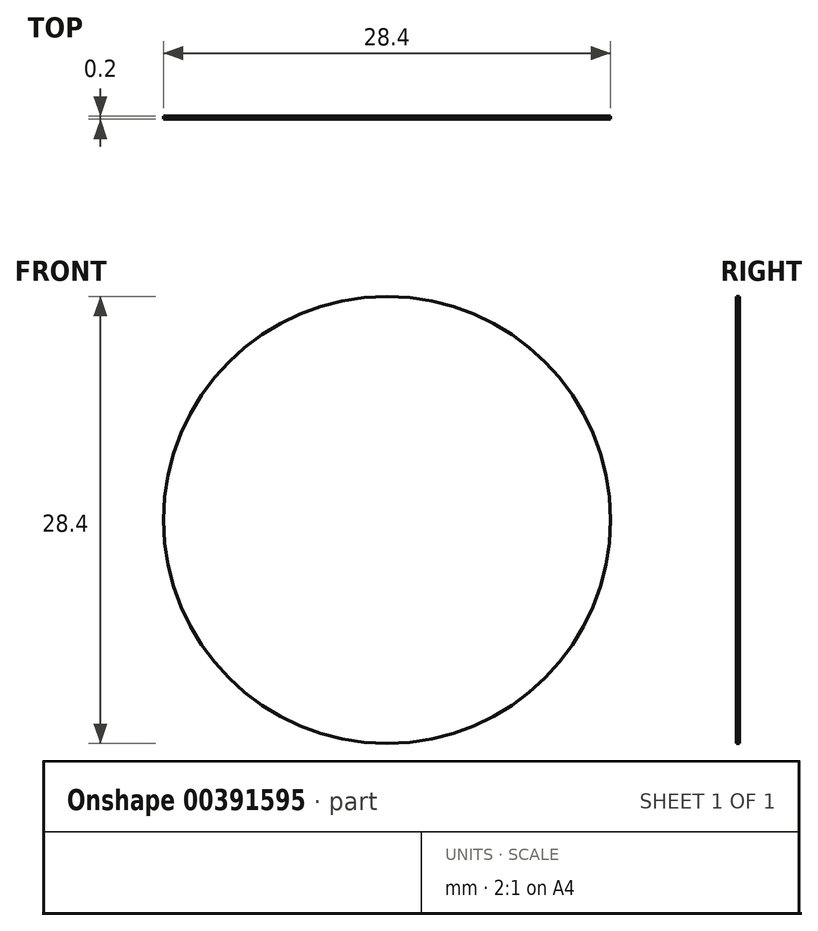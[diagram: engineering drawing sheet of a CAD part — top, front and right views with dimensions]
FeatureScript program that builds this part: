
annotation { "Feature Type Name" : "Feature", "Feature Type Description" : "" }
export const myFeature = defineFeature(function(context is Context, id is Id, definition is map)
    precondition{}
    {
        {
            var Q0;
            Q0=qCreatedBy(makeId("Front.planeOp"),FACE);
            var sketch = newSketch(context, id + "F0", { "sketchPlane" : qUnion([Q0])});
            skCircle(sketch, "E0", {"center": v(0, 0) * mm, "radius": 8 * mm, "construction": true});
            skCircle(sketch, "E1", {"center": v(0, 0) * mm, "radius": 10.5 * mm, "construction": true});
            skLineSegment(sketch, "E2", {"start": v(0, 8) * mm, "end": v(0.75, 8) * mm, "construction": true});
            skLineSegment(sketch, "E3", {"start": v(0.75, 8) * mm, "end": v(0.75, 13.5) * mm, "construction": true});
            skLineSegment(sketch, "E4", {"start": v(0.75, 13.5) * mm, "end": v(0, 13.5) * mm, "construction": true});
            skLineSegment(sketch, "E5", {"start": v(0, 13.5) * mm, "end": v(-0.75, 13.5) * mm, "construction": true});
            skLineSegment(sketch, "E6", {"start": v(-0.75, 13.5) * mm, "end": v(-0.75, 8) * mm, "construction": true});
            skLineSegment(sketch, "E7", {"start": v(-0.75, 8) * mm, "end": v(0, 8) * mm, "construction": true});
            skLineSegment(sketch, "E8.1.0", {"start": v(-3.35, 7.3) * mm, "end": v(-6.1, 12.07) * mm});
            skLineSegment(sketch, "E8.1.1", {"start": v(-7.4, 11.32) * mm, "end": v(-4.65, 6.55) * mm});
            skLineSegment(sketch, "E8.1.2", {"start": v(-4.65, 6.55) * mm, "end": v(-4, 6.93) * mm});
            skLineSegment(sketch, "E8.1.3", {"start": v(-4, 6.93) * mm, "end": v(-3.35, 7.3) * mm});
            skLineSegment(sketch, "E8.1.4", {"start": v(-6.1, 12.07) * mm, "end": v(-6.75, 11.7) * mm});
            skLineSegment(sketch, "E8.1.5", {"start": v(-6.75, 11.7) * mm, "end": v(-7.4, 11.32) * mm});
            skLineSegment(sketch, "E8.2.0", {"start": v(-6.55, 4.65) * mm, "end": v(-11.32, 7.4) * mm});
            skLineSegment(sketch, "E8.2.1", {"start": v(-12.07, 6.1) * mm, "end": v(-7.3, 3.35) * mm});
            skLineSegment(sketch, "E8.2.2", {"start": v(-7.3, 3.35) * mm, "end": v(-6.93, 4) * mm});
            skLineSegment(sketch, "E8.2.3", {"start": v(-6.93, 4) * mm, "end": v(-6.55, 4.65) * mm});
            skLineSegment(sketch, "E8.2.4", {"start": v(-11.32, 7.4) * mm, "end": v(-11.7, 6.75) * mm});
            skLineSegment(sketch, "E8.2.5", {"start": v(-11.7, 6.75) * mm, "end": v(-12.07, 6.1) * mm});
            skLineSegment(sketch, "E8.3.0", {"start": v(-8, 0.75) * mm, "end": v(-13.5, 0.75) * mm, "construction": true});
            skLineSegment(sketch, "E8.3.1", {"start": v(-13.5, -0.75) * mm, "end": v(-8, -0.75) * mm, "construction": true});
            skLineSegment(sketch, "E8.3.2", {"start": v(-8, -0.75) * mm, "end": v(-8, 0) * mm, "construction": true});
            skLineSegment(sketch, "E8.3.3", {"start": v(-8, 0) * mm, "end": v(-8, 0.75) * mm, "construction": true});
            skLineSegment(sketch, "E8.3.4", {"start": v(-13.5, 0.75) * mm, "end": v(-13.5, 0) * mm, "construction": true});
            skLineSegment(sketch, "E8.3.5", {"start": v(-13.5, 0) * mm, "end": v(-13.5, -0.75) * mm, "construction": true});
            skLineSegment(sketch, "E8.4.0", {"start": v(-7.3, -3.35) * mm, "end": v(-12.07, -6.1) * mm});
            skLineSegment(sketch, "E8.4.1", {"start": v(-11.32, -7.4) * mm, "end": v(-6.55, -4.65) * mm});
            skLineSegment(sketch, "E8.4.2", {"start": v(-6.55, -4.65) * mm, "end": v(-6.93, -4) * mm});
            skLineSegment(sketch, "E8.4.3", {"start": v(-6.93, -4) * mm, "end": v(-7.3, -3.35) * mm});
            skLineSegment(sketch, "E8.4.4", {"start": v(-12.07, -6.1) * mm, "end": v(-11.7, -6.75) * mm});
            skLineSegment(sketch, "E8.4.5", {"start": v(-11.7, -6.75) * mm, "end": v(-11.32, -7.4) * mm});
            skLineSegment(sketch, "E8.5.0", {"start": v(-4.65, -6.55) * mm, "end": v(-7.4, -11.32) * mm});
            skLineSegment(sketch, "E8.5.1", {"start": v(-6.1, -12.07) * mm, "end": v(-3.35, -7.3) * mm});
            skLineSegment(sketch, "E8.5.2", {"start": v(-3.35, -7.3) * mm, "end": v(-4, -6.93) * mm});
            skLineSegment(sketch, "E8.5.3", {"start": v(-4, -6.93) * mm, "end": v(-4.65, -6.55) * mm});
            skLineSegment(sketch, "E8.5.4", {"start": v(-7.4, -11.32) * mm, "end": v(-6.75, -11.7) * mm});
            skLineSegment(sketch, "E8.5.5", {"start": v(-6.75, -11.7) * mm, "end": v(-6.1, -12.07) * mm});
            skLineSegment(sketch, "E8.6.0", {"start": v(-0.75, -8) * mm, "end": v(-0.75, -13.5) * mm, "construction": true});
            skLineSegment(sketch, "E8.6.1", {"start": v(0.75, -13.5) * mm, "end": v(0.75, -8) * mm, "construction": true});
            skLineSegment(sketch, "E8.6.2", {"start": v(0.75, -8) * mm, "end": v(0, -8) * mm, "construction": true});
            skLineSegment(sketch, "E8.6.3", {"start": v(0, -8) * mm, "end": v(-0.75, -8) * mm, "construction": true});
            skLineSegment(sketch, "E8.6.4", {"start": v(-0.75, -13.5) * mm, "end": v(0, -13.5) * mm, "construction": true});
            skLineSegment(sketch, "E8.6.5", {"start": v(0, -13.5) * mm, "end": v(0.75, -13.5) * mm, "construction": true});
            skLineSegment(sketch, "E8.7.0", {"start": v(3.35, -7.3) * mm, "end": v(6.1, -12.07) * mm});
            skLineSegment(sketch, "E8.7.1", {"start": v(7.4, -11.32) * mm, "end": v(4.65, -6.55) * mm});
            skLineSegment(sketch, "E8.7.2", {"start": v(4.65, -6.55) * mm, "end": v(4, -6.93) * mm});
            skLineSegment(sketch, "E8.7.3", {"start": v(4, -6.93) * mm, "end": v(3.35, -7.3) * mm});
            skLineSegment(sketch, "E8.7.4", {"start": v(6.1, -12.07) * mm, "end": v(6.75, -11.7) * mm});
            skLineSegment(sketch, "E8.7.5", {"start": v(6.75, -11.7) * mm, "end": v(7.4, -11.32) * mm});
            skLineSegment(sketch, "E8.8.0", {"start": v(6.55, -4.65) * mm, "end": v(11.32, -7.4) * mm});
            skLineSegment(sketch, "E8.8.1", {"start": v(12.07, -6.1) * mm, "end": v(7.3, -3.35) * mm});
            skLineSegment(sketch, "E8.8.2", {"start": v(7.3, -3.35) * mm, "end": v(6.93, -4) * mm});
            skLineSegment(sketch, "E8.8.3", {"start": v(6.93, -4) * mm, "end": v(6.55, -4.65) * mm});
            skLineSegment(sketch, "E8.8.4", {"start": v(11.32, -7.4) * mm, "end": v(11.7, -6.75) * mm});
            skLineSegment(sketch, "E8.8.5", {"start": v(11.7, -6.75) * mm, "end": v(12.07, -6.1) * mm});
            skLineSegment(sketch, "E8.9.0", {"start": v(8, -0.75) * mm, "end": v(13.5, -0.75) * mm, "construction": true});
            skLineSegment(sketch, "E8.9.1", {"start": v(13.5, 0.75) * mm, "end": v(8, 0.75) * mm, "construction": true});
            skLineSegment(sketch, "E8.9.2", {"start": v(8, 0.75) * mm, "end": v(8, 0) * mm, "construction": true});
            skLineSegment(sketch, "E8.9.3", {"start": v(8, 0) * mm, "end": v(8, -0.75) * mm, "construction": true});
            skLineSegment(sketch, "E8.9.4", {"start": v(13.5, -0.75) * mm, "end": v(13.5, 0) * mm, "construction": true});
            skLineSegment(sketch, "E8.9.5", {"start": v(13.5, 0) * mm, "end": v(13.5, 0.75) * mm, "construction": true});
            skLineSegment(sketch, "E8.10.0", {"start": v(7.3, 3.35) * mm, "end": v(12.07, 6.1) * mm});
            skLineSegment(sketch, "E8.10.1", {"start": v(11.32, 7.4) * mm, "end": v(6.55, 4.65) * mm});
            skLineSegment(sketch, "E8.10.2", {"start": v(6.55, 4.65) * mm, "end": v(6.93, 4) * mm});
            skLineSegment(sketch, "E8.10.3", {"start": v(6.93, 4) * mm, "end": v(7.3, 3.35) * mm});
            skLineSegment(sketch, "E8.10.4", {"start": v(12.07, 6.1) * mm, "end": v(11.7, 6.75) * mm});
            skLineSegment(sketch, "E8.10.5", {"start": v(11.7, 6.75) * mm, "end": v(11.32, 7.4) * mm});
            skLineSegment(sketch, "E8.11.0", {"start": v(4.65, 6.55) * mm, "end": v(7.4, 11.32) * mm});
            skLineSegment(sketch, "E8.11.1", {"start": v(6.1, 12.07) * mm, "end": v(3.35, 7.3) * mm});
            skLineSegment(sketch, "E8.11.2", {"start": v(3.35, 7.3) * mm, "end": v(4, 6.93) * mm});
            skLineSegment(sketch, "E8.11.3", {"start": v(4, 6.93) * mm, "end": v(4.65, 6.55) * mm});
            skLineSegment(sketch, "E8.11.4", {"start": v(7.4, 11.32) * mm, "end": v(6.75, 11.7) * mm});
            skLineSegment(sketch, "E8.11.5", {"start": v(6.75, 11.7) * mm, "end": v(6.1, 12.07) * mm});
            skCircle(sketch, "E9", {"center": v(0, 0) * mm, "radius": 13.5 * mm, "construction": true});
            skSolve(sketch);
        }
        {
            var Q0;
            Q0=qCreatedBy(makeId("Front.planeOp"),FACE);
            var sketch = newSketch(context, id + "F1", { "sketchPlane" : qUnion([Q0])});
            skText(sketch, "E10", { "text": "12", "fontName": "AllertaStencil-Regular.ttf"});
            skText(sketch, "E11", { "text": "6", "fontName": "AllertaStencil-Regular.ttf"});
            skText(sketch, "E12", { "text": "9", "fontName": "AllertaStencil-Regular.ttf"});
            skPoint(sketch, "E13", {"position": v(-9.75, 0) * mm});
            skText(sketch, "E14", { "text": "3", "fontName": "AllertaStencil-Regular.ttf"});
            skCircle(sketch, "E15", {"center": v(0, 0) * mm, "radius": 9.75 * mm, "construction": true});
            skCircle(sketch, "E16", {"center": v(0, 0) * mm, "radius": 6 * mm, "construction": true});
            skLineSegment(sketch, "E17", {"start": v(0, 0) * mm, "end": v(0, 9.75) * mm, "construction": true});
            skLineSegment(sketch, "E18.1.0", {"start": v(0, 0) * mm, "end": v(-9.75, 0) * mm, "construction": true});
            skLineSegment(sketch, "E18.2.0", {"start": v(0, 0) * mm, "end": v(0, -9.75) * mm, "construction": true});
            skLineSegment(sketch, "E18.3.0", {"start": v(0, 0) * mm, "end": v(9.75, 0) * mm, "construction": true});
            skPoint(sketch, "E19", {"position": v(9.75, 0) * mm});
            const initialGuessF1  = {"E10": [-0.00263, 0.006, 1, 0, 0.00375], "E11": [-0.00164, -0.00975, 1, 0, 0.00375], "E12": [-0.00975, -0.00188, 1, 0, 0.00375], "E14": [0.00681, -0.00187, 1, 0, 0.00375]};
            skSetInitialGuess(sketch, initialGuessF1);
            skSolve(sketch);
        }
        {
            var Q0;
            Q0=qCreatedBy(makeId("Front.planeOp"),FACE);
            var sketch = newSketch(context, id + "F2", { "sketchPlane" : qUnion([Q0])});
            skLineSegment(sketch, "E20", {"start": v(0, 10.06) * mm, "end": v(2, 13.53) * mm});
            skLineSegment(sketch, "E21", {"start": v(2, 13.53) * mm, "end": v(-2, 13.53) * mm});
            skLineSegment(sketch, "E22", {"start": v(-2, 13.53) * mm, "end": v(0, 10.06) * mm});
            skLineSegment(sketch, "E23", {"start": v(-10.44, 0) * mm, "end": v(-10.44, 1.25) * mm});
            skLineSegment(sketch, "E24", {"start": v(-10.44, 1.25) * mm, "end": v(-13.44, 1.25) * mm});
            skLineSegment(sketch, "E25", {"start": v(-13.44, 1.25) * mm, "end": v(-13.44, -1.25) * mm});
            skLineSegment(sketch, "E26", {"start": v(-13.44, -1.25) * mm, "end": v(-10.44, -1.25) * mm});
            skLineSegment(sketch, "E27", {"start": v(-10.44, -1.25) * mm, "end": v(-10.44, 0) * mm});
            skCircle(sketch, "E28", {"center": v(0, 0) * mm, "radius": 11.25 * mm, "construction": true});
            skLineSegment(sketch, "E29.1.0", {"start": v(-1.25, -10.44) * mm, "end": v(-1.25, -13.44) * mm});
            skLineSegment(sketch, "E29.1.1", {"start": v(-1.25, -13.44) * mm, "end": v(1.25, -13.44) * mm});
            skLineSegment(sketch, "E29.1.2", {"start": v(1.25, -13.44) * mm, "end": v(1.25, -10.44) * mm});
            skLineSegment(sketch, "E29.1.3", {"start": v(1.25, -10.44) * mm, "end": v(0, -10.44) * mm});
            skLineSegment(sketch, "E29.1.4", {"start": v(0, -10.44) * mm, "end": v(-1.25, -10.44) * mm});
            skLineSegment(sketch, "E29.2.0", {"start": v(10.44, -1.25) * mm, "end": v(13.44, -1.25) * mm});
            skLineSegment(sketch, "E29.2.1", {"start": v(13.44, -1.25) * mm, "end": v(13.44, 1.25) * mm});
            skLineSegment(sketch, "E29.2.2", {"start": v(13.44, 1.25) * mm, "end": v(10.44, 1.25) * mm});
            skLineSegment(sketch, "E29.2.3", {"start": v(10.44, 1.25) * mm, "end": v(10.44, 0) * mm});
            skLineSegment(sketch, "E29.2.4", {"start": v(10.44, 0) * mm, "end": v(10.44, -1.25) * mm});
            skLineSegment(sketch, "E29.anchor1", {"start": v(0, 0) * mm, "end": v(-10.44, 0) * mm, "construction": true});
            skLineSegment(sketch, "E29.anchor2", {"start": v(0, 0) * mm, "end": v(10.44, 0) * mm, "construction": true});
            skCircle(sketch, "E30", {"center": v(0, 0) * mm, "radius": 14.2 * mm, "construction": true});
            skCircle(sketch, "E31", {"center": v(0, 0) * mm, "radius": 13.5 * mm, "construction": true});
            skLineSegment(sketch, "E32", {"start": v(0, 13.5) * mm, "end": v(0, 11.25) * mm, "construction": true});
            skCircle(sketch, "E33", {"center": v(0, 12.38) * mm, "radius": 1.13 * mm, "construction": true});
            skCircle(sketch, "E34.1.0", {"center": v(-6.19, 10.72) * mm, "radius": 1.13 * mm, "construction": true});
            skCircle(sketch, "E34.2.0", {"center": v(-10.72, 6.19) * mm, "radius": 1.13 * mm, "construction": true});
            skCircle(sketch, "E34.3.0", {"center": v(-12.38, 0) * mm, "radius": 1.13 * mm, "construction": true});
            skCircle(sketch, "E34.4.0", {"center": v(-10.72, -6.19) * mm, "radius": 1.13 * mm, "construction": true});
            skCircle(sketch, "E34.5.0", {"center": v(-6.19, -10.72) * mm, "radius": 1.13 * mm, "construction": true});
            skCircle(sketch, "E34.6.0", {"center": v(0, -12.38) * mm, "radius": 1.13 * mm, "construction": true});
            skCircle(sketch, "E34.7.0", {"center": v(6.19, -10.72) * mm, "radius": 1.13 * mm, "construction": true});
            skCircle(sketch, "E34.8.0", {"center": v(10.72, -6.19) * mm, "radius": 1.13 * mm, "construction": true});
            skCircle(sketch, "E34.9.0", {"center": v(12.38, 0) * mm, "radius": 1.13 * mm, "construction": true});
            skCircle(sketch, "E34.10.0", {"center": v(10.72, 6.19) * mm, "radius": 1.13 * mm, "construction": true});
            skCircle(sketch, "E34.11.0", {"center": v(6.19, 10.72) * mm, "radius": 1.13 * mm, "construction": true});
            skSolve(sketch);
        }
        {
            var Q0;
            Q0=qCreatedBy(makeId("Front.planeOp"),FACE);
            var sketch = newSketch(context, id + "F3", { "sketchPlane" : qUnion([Q0])});
            skCircle(sketch, "E35", {"center": v(0, 0) * mm, "radius": 14.2 * mm});
            skSolve(sketch);
        }
        {
            var Q0;
            Q0=qCreatedBy(makeId("Front.planeOp"),FACE);
            var sketch = newSketch(context, id + "F4", { "sketchPlane" : qUnion([Q0])});
            skArc(sketch, "E36", {"start": v(-2.54, 3.8) * mm, "mid": v(-2.64, 3.7) * mm, "end": v(-2.56, 3.6) * mm});
            skCircle(sketch, "E37", {"center": v(-1.1, 2.95) * mm, "radius": 0.5 * mm});
            skCircle(sketch, "E38", {"center": v(-1.1, 2.95) * mm, "radius": 0.3 * mm});
            skArc(sketch, "E39", {"start": v(0.45, 3.23) * mm, "mid": v(-0.45, 3.04) * mm, "end": v(0.32, 2.53) * mm});
            skArc(sketch, "E40", {"start": v(0.29, 3.12) * mm, "mid": v(-0.25, 3) * mm, "end": v(0.2, 2.7) * mm});
            skCircle(sketch, "E41", {"center": v(1.84, 2.95) * mm, "radius": 0.5 * mm});
            skCircle(sketch, "E42", {"center": v(1.84, 2.95) * mm, "radius": 0.3 * mm});
            skLineSegment(sketch, "E43", {"start": v(-1.1, 2.95) * mm, "end": v(0.04, 2.95) * mm, "construction": true});
            skLineSegment(sketch, "E44", {"start": v(0.94, 2.95) * mm, "end": v(1.84, 2.95) * mm, "construction": true});
            skLineSegment(sketch, "E45", {"start": v(0.94, 2.95) * mm, "end": v(0.04, 2.95) * mm, "construction": true});
            skLineSegment(sketch, "E46", {"start": v(0.04, 3.45) * mm, "end": v(-1.1, 3.45) * mm, "construction": true});
            skLineSegment(sketch, "E47", {"start": v(-1.1, 2.45) * mm, "end": v(0.04, 2.45) * mm, "construction": true});
            skLineSegment(sketch, "E48", {"start": v(0.04, 2.45) * mm, "end": v(1.84, 2.45) * mm, "construction": true});
            skArc(sketch, "E49", {"start": v(0.64, 3.45) * mm, "mid": v(0.54, 3.35) * mm, "end": v(0.64, 3.25) * mm});
            skArc(sketch, "E50", {"start": v(1.24, 3.25) * mm, "mid": v(1.34, 3.35) * mm, "end": v(1.24, 3.45) * mm});
            skArc(sketch, "E51", {"start": v(0.7, 2.57) * mm, "mid": v(0.79, 2.45) * mm, "end": v(0.9, 2.53) * mm});
            skCircle(sketch, "E52", {"center": v(2.52, 2.55) * mm, "radius": 0.1 * mm});
            skCircle(sketch, "E53", {"center": v(3.31, 3.36) * mm, "radius": 0.1 * mm});
            skCircle(sketch, "E54", {"center": v(3.22, 2.55) * mm, "radius": 0.1 * mm});
            skArc(sketch, "E55", {"start": v(0.29, 3.12) * mm, "mid": v(0.43, 3.1) * mm, "end": v(0.45, 3.23) * mm});
            skArc(sketch, "E56", {"start": v(0.32, 2.53) * mm, "mid": v(0.34, 2.67) * mm, "end": v(0.2, 2.7) * mm});
            skArc(sketch, "E57", {"start": v(-2.76, 2.57) * mm, "mid": v(-2.74, 2.48) * mm, "end": v(-2.66, 2.45) * mm});
            skArc(sketch, "E58", {"start": v(-2.16, 2.65) * mm, "mid": v(-1.93, 2.87) * mm, "end": v(-2.16, 3.1) * mm});
            skArc(sketch, "E59", {"start": v(-2.16, 3.3) * mm, "mid": v(-2, 3.45) * mm, "end": v(-2.16, 3.6) * mm});
            skArc(sketch, "E60", {"start": v(-1.9, 3.2) * mm, "mid": v(-1.84, 3.59) * mm, "end": v(-2.16, 3.8) * mm});
            skLineSegment(sketch, "E61", {"start": v(-1.1, 2.45) * mm, "end": v(-2.66, 2.45) * mm, "construction": true});
            skLineSegment(sketch, "E62", {"start": v(-2.66, 2.45) * mm, "end": v(-2.16, 2.45) * mm});
            skLineSegment(sketch, "E63", {"start": v(-2.56, 3.6) * mm, "end": v(-2.76, 2.57) * mm});
            skLineSegment(sketch, "E64", {"start": v(-2.54, 3.8) * mm, "end": v(-2.16, 3.8) * mm});
            skLineSegment(sketch, "E65", {"start": v(-1.6, 3.8) * mm, "end": v(2.75, 3.8) * mm});
            skLineSegment(sketch, "E66", {"start": v(2.84, 3.68) * mm, "end": v(2.69, 2.86) * mm});
            skLineSegment(sketch, "E67", {"start": v(2.69, 2.86) * mm, "end": v(3.24, 3.43) * mm});
            skLineSegment(sketch, "E68", {"start": v(3.38, 3.3) * mm, "end": v(3.1, 3) * mm});
            skLineSegment(sketch, "E69", {"start": v(3.1, 3) * mm, "end": v(3.31, 2.6) * mm});
            skLineSegment(sketch, "E70", {"start": v(3.14, 2.5) * mm, "end": v(2.95, 2.84) * mm});
            skLineSegment(sketch, "E71", {"start": v(2.95, 2.84) * mm, "end": v(2.6, 2.48) * mm});
            skLineSegment(sketch, "E72", {"start": v(2.42, 2.57) * mm, "end": v(2.63, 3.6) * mm});
            skLineSegment(sketch, "E73", {"start": v(2.63, 3.6) * mm, "end": v(-1.6, 3.6) * mm});
            skArc(sketch, "E74", {"start": v(-1.6, 3.8) * mm, "mid": v(-1.7, 3.7) * mm, "end": v(-1.6, 3.6) * mm});
            skLineSegment(sketch, "E75", {"start": v(0.64, 3.45) * mm, "end": v(1.24, 3.45) * mm});
            skLineSegment(sketch, "E76", {"start": v(0.64, 3.25) * mm, "end": v(0.84, 3.25) * mm});
            skLineSegment(sketch, "E77", {"start": v(0.84, 3.25) * mm, "end": v(0.7, 2.57) * mm});
            skLineSegment(sketch, "E78", {"start": v(0.9, 2.53) * mm, "end": v(1.04, 3.25) * mm});
            skLineSegment(sketch, "E79", {"start": v(1.04, 3.25) * mm, "end": v(1.24, 3.25) * mm});
            skLineSegment(sketch, "E80", {"start": v(1.84, 2.45) * mm, "end": v(2.52, 2.45) * mm, "construction": true});
            skLineSegment(sketch, "E81", {"start": v(2.52, 2.45) * mm, "end": v(3.22, 2.45) * mm, "construction": true});
            skLineSegment(sketch, "E82", {"start": v(2.52, 2.55) * mm, "end": v(3.31, 3.36) * mm, "construction": true});
            skArc(sketch, "E83", {"start": v(2.84, 3.68) * mm, "mid": v(2.82, 3.76) * mm, "end": v(2.75, 3.8) * mm});
            skLineSegment(sketch, "E84", {"start": v(1.24, 3.45) * mm, "end": v(1.84, 3.45) * mm, "construction": true});
            skLineSegment(sketch, "E85", {"start": v(0.26, 2.61) * mm, "end": v(0.37, 3.17) * mm, "construction": true});
            skLineSegment(sketch, "E86", {"start": v(0.84, 3.25) * mm, "end": v(1.04, 3.25) * mm, "construction": true});
            skLineSegment(sketch, "E87", {"start": v(0.64, 3.35) * mm, "end": v(1.24, 3.35) * mm, "construction": true});
            skPoint(sketch, "E88", {"position": v(0.94, 3.35) * mm});
            skPoint(sketch, "E89", {"position": v(0.94, 3.25) * mm});
            skLineSegment(sketch, "E90", {"start": v(-2.54, 2.65) * mm, "end": v(-2.45, 3.1) * mm});
            skLineSegment(sketch, "E91", {"start": v(-2.35, 3.6) * mm, "end": v(-2.16, 3.6) * mm});
            skLineSegment(sketch, "E92", {"start": v(-2.41, 3.3) * mm, "end": v(-2.16, 3.3) * mm});
            skLineSegment(sketch, "E93", {"start": v(-2.16, 3.1) * mm, "end": v(-2.45, 3.1) * mm});
            skLineSegment(sketch, "E94", {"start": v(-2.54, 2.65) * mm, "end": v(-2.16, 2.65) * mm});
            skLineSegment(sketch, "E95.trimOffspring", {"start": v(-2.41, 3.3) * mm, "end": v(-2.35, 3.6) * mm});
            skArc(sketch, "E96.trimOffspring", {"start": v(-2.16, 2.45) * mm, "mid": v(-1.76, 2.74) * mm, "end": v(-1.9, 3.2) * mm});
            skSolve(sketch);
        }
        {
            var Q0;
            Q0=qSketchRegion(id+"F3",true);
            extrude(context, id + "F5", {"entities" : qUnion([Q0]), "depth" : 0.2 * mm});
        }
    });
